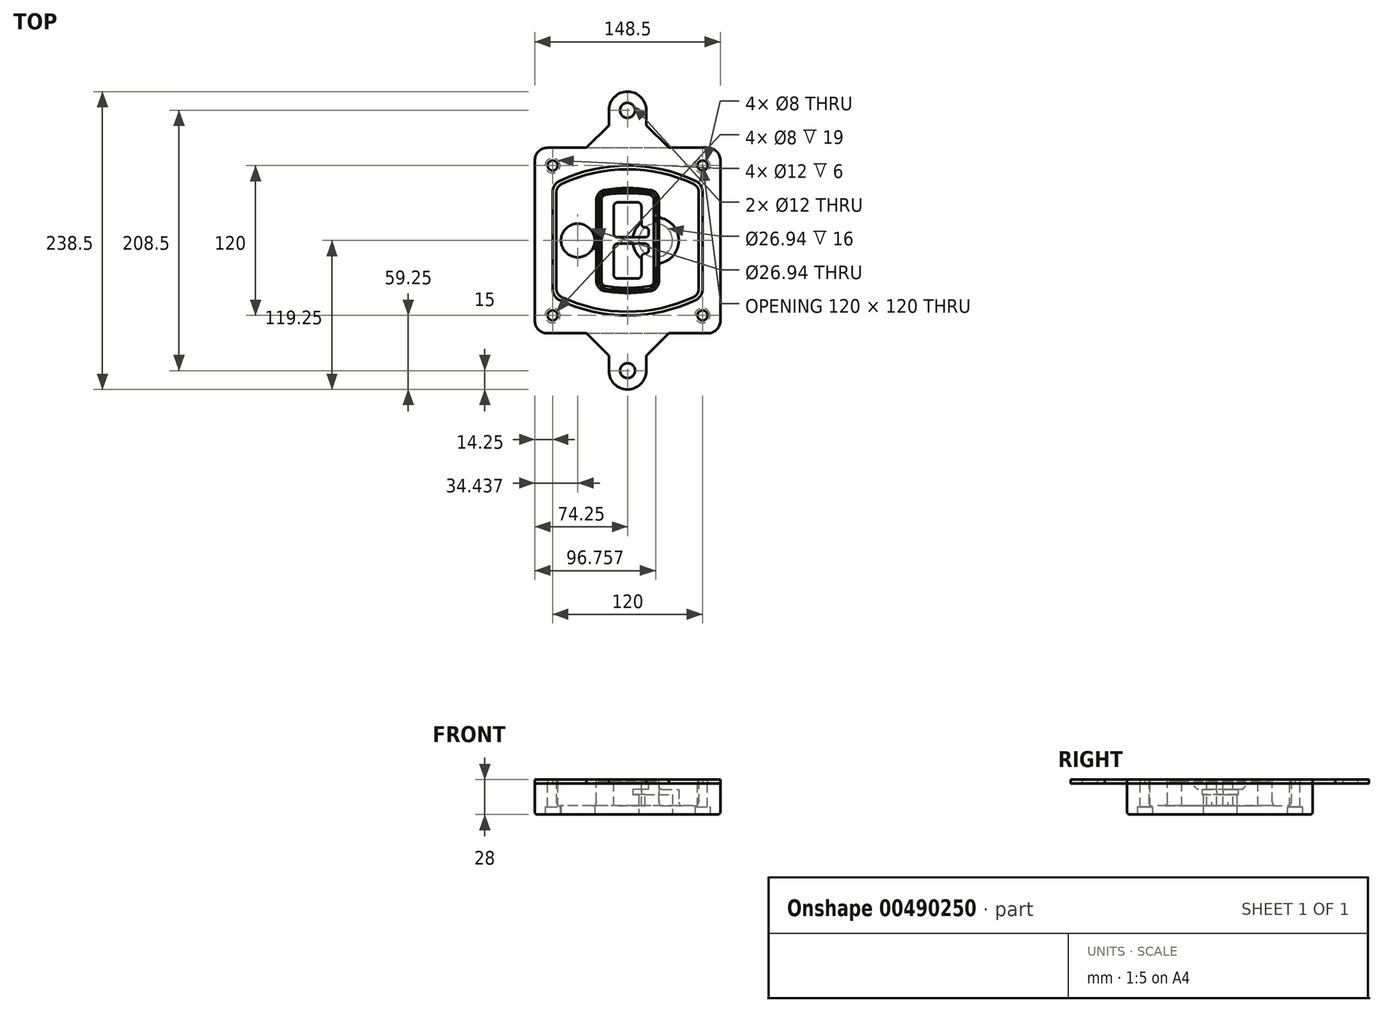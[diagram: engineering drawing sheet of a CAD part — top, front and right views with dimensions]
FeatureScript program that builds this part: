
annotation { "Feature Type Name" : "Feature", "Feature Type Description" : "" }
export const myFeature = defineFeature(function(context is Context, id is Id, definition is map)
    precondition{}
    {
        {
            var Q0;
            Q0=qCreatedBy(makeId("Top.planeOp"),FACE);
            var sketch = newSketch(context, id + "F0", { "sketchPlane" : qUnion([Q0])});
            skPoint(sketch, "E0.rect.middle", {"position": v(0, 0) * mm});
            skLineSegment(sketch, "E1.bottom", {"start": v(-64.25, -74.25) * mm, "end": v(64.25, -74.25) * mm});
            skLineSegment(sketch, "E1.top", {"start": v(-64.25, 74.25) * mm, "end": v(64.25, 74.25) * mm});
            skLineSegment(sketch, "E1.left", {"start": v(-74.25, -64.25) * mm, "end": v(-74.25, 64.25) * mm});
            skLineSegment(sketch, "E1.right", {"start": v(74.25, -64.25) * mm, "end": v(74.25, 64.25) * mm});
            skLineSegment(sketch, "E2", {"start": v(-74.25, 74.25) * mm, "end": v(74.25, -74.25) * mm, "construction": true});
            skLineSegment(sketch, "E3", {"start": v(74.25, 74.25) * mm, "end": v(-74.25, -74.25) * mm, "construction": true});
            skCircle(sketch, "E4", {"center": v(-60, 60) * mm, "radius": 4 * mm});
            skCircle(sketch, "E5", {"center": v(60, 60) * mm, "radius": 4 * mm});
            skCircle(sketch, "E6", {"center": v(60, -60) * mm, "radius": 4 * mm});
            skCircle(sketch, "E7", {"center": v(-60, -60) * mm, "radius": 4 * mm});
            skLineSegment(sketch, "E8", {"start": v(-60, 60) * mm, "end": v(60, 60) * mm, "construction": true});
            skLineSegment(sketch, "E9", {"start": v(60, 60) * mm, "end": v(60, -60) * mm, "construction": true});
            skLineSegment(sketch, "E10", {"start": v(60, -60) * mm, "end": v(-60, -60) * mm, "construction": true});
            skLineSegment(sketch, "E11", {"start": v(-60, -60) * mm, "end": v(-60, 60) * mm, "construction": true});
            skLineSegment(sketch, "E12", {"start": v(-60, 38.83) * mm, "end": v(-60, -38.83) * mm});
            skLineSegment(sketch, "E13", {"start": v(60, 38.83) * mm, "end": v(60, -38.83) * mm});
            skArc(sketch, "E14", {"start": v(54.26, 47.88) * mm, "mid": v(0, 60) * mm, "end": v(-54.26, 47.88) * mm});
            skArc(sketch, "E15", {"start": v(-54.26, -47.88) * mm, "mid": v(0, -60) * mm, "end": v(54.26, -47.88) * mm});
            skLineSegment(sketch, "E16", {"start": v(-60, 0) * mm, "end": v(60, 0) * mm, "construction": true});
            skPoint(sketch, "E17.visualSharp", {"position": v(-60, -45) * mm});
            skArc(sketch, "E17.filletArc", {"start": v(-60, -38.83) * mm, "mid": v(-58.44, -44.2) * mm, "end": v(-54.26, -47.88) * mm});
            skPoint(sketch, "E18.visualSharp", {"position": v(-60, 45) * mm});
            skArc(sketch, "E18.filletArc", {"start": v(-54.26, 47.88) * mm, "mid": v(-58.44, 44.2) * mm, "end": v(-60, 38.83) * mm});
            skPoint(sketch, "E19.visualSharp", {"position": v(60, 45) * mm});
            skArc(sketch, "E19.filletArc", {"start": v(60, 38.83) * mm, "mid": v(58.44, 44.2) * mm, "end": v(54.26, 47.88) * mm});
            skPoint(sketch, "E20.visualSharp", {"position": v(60, -45) * mm});
            skArc(sketch, "E20.filletArc", {"start": v(54.26, -47.88) * mm, "mid": v(58.44, -44.2) * mm, "end": v(60, -38.83) * mm});
            skPoint(sketch, "E21.visualSharp", {"position": v(-74.25, 74.25) * mm});
            skArc(sketch, "E21.filletArc", {"start": v(-64.25, 74.25) * mm, "mid": v(-71.32, 71.32) * mm, "end": v(-74.25, 64.25) * mm});
            skPoint(sketch, "E22.visualSharp", {"position": v(74.25, 74.25) * mm});
            skArc(sketch, "E22.filletArc", {"start": v(74.25, 64.25) * mm, "mid": v(71.32, 71.32) * mm, "end": v(64.25, 74.25) * mm});
            skPoint(sketch, "E23.visualSharp", {"position": v(74.25, -74.25) * mm});
            skArc(sketch, "E23.filletArc", {"start": v(64.25, -74.25) * mm, "mid": v(71.32, -71.32) * mm, "end": v(74.25, -64.25) * mm});
            skPoint(sketch, "E24.visualSharp", {"position": v(-74.25, -74.25) * mm});
            skArc(sketch, "E24.filletArc", {"start": v(-74.25, -64.25) * mm, "mid": v(-71.32, -71.32) * mm, "end": v(-64.25, -74.25) * mm});
            skArc(sketch, "E25.0", {"start": v(57, 38.83) * mm, "mid": v(55.9, 42.58) * mm, "end": v(52.98, 45.17) * mm});
            skLineSegment(sketch, "E25.1", {"start": v(57, 38.83) * mm, "end": v(57, -38.83) * mm});
            skArc(sketch, "E25.2", {"start": v(52.98, -45.17) * mm, "mid": v(55.9, -42.58) * mm, "end": v(57, -38.83) * mm});
            skArc(sketch, "E25.3", {"start": v(-52.98, -45.17) * mm, "mid": v(0, -57) * mm, "end": v(52.98, -45.17) * mm});
            skArc(sketch, "E25.4", {"start": v(-57, -38.83) * mm, "mid": v(-55.9, -42.58) * mm, "end": v(-52.98, -45.17) * mm});
            skArc(sketch, "E25.5", {"start": v(52.98, 45.17) * mm, "mid": v(0, 57) * mm, "end": v(-52.98, 45.17) * mm});
            skLineSegment(sketch, "E25.6", {"start": v(-57, 38.83) * mm, "end": v(-57, -38.83) * mm});
            skArc(sketch, "E25.7", {"start": v(-52.98, 45.17) * mm, "mid": v(-55.9, 42.58) * mm, "end": v(-57, 38.83) * mm});
            skArc(sketch, "E26.0", {"start": v(-55.96, 51.5) * mm, "mid": v(-61.82, 46.33) * mm, "end": v(-64, 38.83) * mm});
            skArc(sketch, "E26.1", {"start": v(55.96, 51.5) * mm, "mid": v(0, 64) * mm, "end": v(-55.96, 51.5) * mm});
            skArc(sketch, "E26.2", {"start": v(64, 38.83) * mm, "mid": v(61.82, 46.33) * mm, "end": v(55.96, 51.5) * mm});
            skLineSegment(sketch, "E26.3", {"start": v(64, 38.83) * mm, "end": v(64, -38.83) * mm});
            skArc(sketch, "E26.4", {"start": v(55.96, -51.5) * mm, "mid": v(61.82, -46.33) * mm, "end": v(64, -38.83) * mm});
            skLineSegment(sketch, "E26.5", {"start": v(-64, 38.83) * mm, "end": v(-64, -38.83) * mm});
            skArc(sketch, "E26.6", {"start": v(-55.96, -51.5) * mm, "mid": v(0, -64) * mm, "end": v(55.96, -51.5) * mm});
            skArc(sketch, "E26.7", {"start": v(-64, -38.83) * mm, "mid": v(-61.82, -46.33) * mm, "end": v(-55.96, -51.5) * mm});
            skSolve(sketch);
        }
        {
            var Q0;
            Q0=makeQuery(id+"F0.imprint","IMPRINT",FACE,{"disambiguationData":[TD([[makeQuery(id+"F0.imprint","IMPRINT",EDGE,{"derivedFrom":sQuery(id+"F0.wireOp",EDGE,"E1.bottom")}),1.0]])]});
            var Q1;
            Q1=makeQuery(id+"F0.imprint","IMPRINT",FACE,{"disambiguationData":[TD([[makeQuery(id+"F0.imprint","IMPRINT",EDGE,{"derivedFrom":sQuery(id+"F0.wireOp",EDGE,"E12")}),1.0]])]});
            var Q2;
            Q2=makeQuery(id+"F0.imprint","IMPRINT",FACE,{"disambiguationData":[TD([[makeQuery(id+"F0.imprint","IMPRINT",EDGE,{"derivedFrom":sQuery(id+"F0.wireOp",EDGE,"E25.0")}),1.0]])]});
            var Q3;
            Q3=makeQuery(id+"F0.imprint","IMPRINT",FACE,{"disambiguationData":[TD([[makeQuery(id+"F0.imprint","IMPRINT",EDGE,{"derivedFrom":sQuery(id+"F0.wireOp",EDGE,"E12")}),-1.0]])]});
            extrude(context, id + "F1", {"entities" : qUnion([Q0, Q1, Q2, Q3]), "oppositeDirection" : true, "depth" : 25 * mm});
        }
        {
            var Q0;
            Q0=makeQuery(id+"F0.imprint","IMPRINT",FACE,{"disambiguationData":[TD([[makeQuery(id+"F0.imprint","IMPRINT",EDGE,{"derivedFrom":sQuery(id+"F0.wireOp",EDGE,"E12")}),1.0]])]});
            extrude(context, id + "F2", {"entities" : qUnion([Q0]), "operationType" : NewBodyOperationType.ADD, "depth" : 3 * mm});
        }
        {
            var Q0;
            Q0=makeQuery(id+"F0.imprint","IMPRINT",FACE,{"disambiguationData":[TD([[makeQuery(id+"F0.imprint","IMPRINT",EDGE,{"derivedFrom":sQuery(id+"F0.wireOp",EDGE,"E25.0")}),1.0]])]});
            extrude(context, id + "F3", {"entities" : qUnion([Q0]), "operationType" : NewBodyOperationType.REMOVE, "oppositeDirection" : true, "depth" : 18 * mm});
        }
        {
            var Q0;
            Q0=makeQuery(id+"F2.opExtrude","CAP_FACE",FACE,{"disambiguationData":[OSD([sQuery(id+"F0.wireOp",EDGE,"E12"),sQuery(id+"F0.wireOp",EDGE,"E13"),sQuery(id+"F0.wireOp",EDGE,"E14"),sQuery(id+"F0.wireOp",EDGE,"E15"),sQuery(id+"F0.wireOp",EDGE,"E17.filletArc"),sQuery(id+"F0.wireOp",EDGE,"E18.filletArc"),sQuery(id+"F0.wireOp",EDGE,"E19.filletArc"),sQuery(id+"F0.wireOp",EDGE,"E20.filletArc"),sQuery(id+"F0.wireOp",EDGE,"E25.0"),sQuery(id+"F0.wireOp",EDGE,"E25.1"),sQuery(id+"F0.wireOp",EDGE,"E25.2"),sQuery(id+"F0.wireOp",EDGE,"E25.3"),sQuery(id+"F0.wireOp",EDGE,"E25.4"),sQuery(id+"F0.wireOp",EDGE,"E25.5"),sQuery(id+"F0.wireOp",EDGE,"E25.6"),sQuery(id+"F0.wireOp",EDGE,"E25.7")])],"isStart":false});
            var sketch = newSketch(context, id + "F4", { "sketchPlane" : qUnion([Q0])});
            skArc(sketch, "E27.0", {"start": v(-18.34, -40.45) * mm, "mid": v(0, -42) * mm, "end": v(18.34, -40.45) * mm});
            skArc(sketch, "E28.0", {"start": v(18.34, 40.45) * mm, "mid": v(0, 42) * mm, "end": v(-18.34, 40.45) * mm});
            skLineSegment(sketch, "E29", {"start": v(-25, 32.57) * mm, "end": v(-25, -32.57) * mm});
            skLineSegment(sketch, "E30", {"start": v(25, 32.57) * mm, "end": v(25, -32.57) * mm});
            skLineSegment(sketch, "E31", {"start": v(-25, 39.1) * mm, "end": v(25, 39.1) * mm, "construction": true});
            skLineSegment(sketch, "E32", {"start": v(-25, -39.1) * mm, "end": v(25, -39.1) * mm, "construction": true});
            skPoint(sketch, "E33.visualSharp", {"position": v(-25, 39.1) * mm});
            skArc(sketch, "E33.filletArc", {"start": v(-18.34, 40.45) * mm, "mid": v(-23.11, 37.73) * mm, "end": v(-25, 32.57) * mm});
            skPoint(sketch, "E34.visualSharp", {"position": v(25, 39.1) * mm});
            skArc(sketch, "E34.filletArc", {"start": v(25, 32.57) * mm, "mid": v(23.11, 37.73) * mm, "end": v(18.34, 40.45) * mm});
            skPoint(sketch, "E35.visualSharp", {"position": v(25, -39.1) * mm});
            skArc(sketch, "E35.filletArc", {"start": v(18.34, -40.45) * mm, "mid": v(23.11, -37.73) * mm, "end": v(25, -32.57) * mm});
            skPoint(sketch, "E36.visualSharp", {"position": v(-25, -39.1) * mm});
            skArc(sketch, "E36.filletArc", {"start": v(-25, -32.57) * mm, "mid": v(-23.11, -37.73) * mm, "end": v(-18.34, -40.45) * mm});
            skArc(sketch, "E37.0", {"start": v(52.98, 45.17) * mm, "mid": v(0, 57) * mm, "end": v(-52.98, 45.17) * mm});
            skArc(sketch, "E37.1", {"start": v(-52.98, 45.17) * mm, "mid": v(-55.9, 42.58) * mm, "end": v(-57, 38.83) * mm});
            skLineSegment(sketch, "E37.2", {"start": v(-57, 38.83) * mm, "end": v(-57, -38.83) * mm});
            skArc(sketch, "E37.3", {"start": v(-57, -38.83) * mm, "mid": v(-55.9, -42.58) * mm, "end": v(-52.98, -45.17) * mm});
            skArc(sketch, "E37.4", {"start": v(-52.98, -45.17) * mm, "mid": v(0, -57) * mm, "end": v(52.98, -45.17) * mm});
            skArc(sketch, "E37.5", {"start": v(52.98, -45.17) * mm, "mid": v(55.9, -42.58) * mm, "end": v(57, -38.83) * mm});
            skLineSegment(sketch, "E37.6", {"start": v(57, 38.83) * mm, "end": v(57, -38.83) * mm});
            skArc(sketch, "E37.7", {"start": v(57, 38.83) * mm, "mid": v(55.9, 42.58) * mm, "end": v(52.98, 45.17) * mm});
            skLineSegment(sketch, "E38.0", {"start": v(23, 32.57) * mm, "end": v(23, -32.57) * mm});
            skArc(sketch, "E38.1", {"start": v(18, -38.48) * mm, "mid": v(21.58, -36.44) * mm, "end": v(23, -32.57) * mm});
            skArc(sketch, "E38.2", {"start": v(-18, -38.48) * mm, "mid": v(0, -40) * mm, "end": v(18, -38.48) * mm});
            skArc(sketch, "E38.3", {"start": v(-23, -32.57) * mm, "mid": v(-21.58, -36.44) * mm, "end": v(-18, -38.48) * mm});
            skLineSegment(sketch, "E38.4", {"start": v(-23, 32.57) * mm, "end": v(-23, -32.57) * mm});
            skArc(sketch, "E38.5", {"start": v(23, 32.57) * mm, "mid": v(21.58, 36.44) * mm, "end": v(18, 38.48) * mm});
            skArc(sketch, "E38.6", {"start": v(-18, 38.48) * mm, "mid": v(-21.58, 36.44) * mm, "end": v(-23, 32.57) * mm});
            skArc(sketch, "E38.7", {"start": v(18, 38.48) * mm, "mid": v(0, 40) * mm, "end": v(-18, 38.48) * mm});
            skArc(sketch, "E39.0", {"start": v(21, 32.57) * mm, "mid": v(20.06, 35.15) * mm, "end": v(17.67, 36.5) * mm});
            skLineSegment(sketch, "E39.1", {"start": v(21, 32.57) * mm, "end": v(21, -32.57) * mm});
            skArc(sketch, "E39.2", {"start": v(17.67, -36.5) * mm, "mid": v(20.06, -35.15) * mm, "end": v(21, -32.57) * mm});
            skArc(sketch, "E39.3", {"start": v(-17.67, -36.5) * mm, "mid": v(0, -38) * mm, "end": v(17.67, -36.5) * mm});
            skArc(sketch, "E39.4", {"start": v(-21, -32.57) * mm, "mid": v(-20.06, -35.15) * mm, "end": v(-17.67, -36.5) * mm});
            skArc(sketch, "E39.5", {"start": v(17.67, 36.5) * mm, "mid": v(0, 38) * mm, "end": v(-17.67, 36.5) * mm});
            skLineSegment(sketch, "E39.6", {"start": v(-21, 32.57) * mm, "end": v(-21, -32.57) * mm});
            skArc(sketch, "E39.7", {"start": v(-17.67, 36.5) * mm, "mid": v(-20.06, 35.15) * mm, "end": v(-21, 32.57) * mm});
            skLineSegment(sketch, "E40", {"start": v(-25, 0) * mm, "end": v(25, 0) * mm, "construction": true});
            skLineSegment(sketch, "E41", {"start": v(-11, 5.5) * mm, "end": v(-11, 27.5) * mm});
            skLineSegment(sketch, "E42", {"start": v(-8, 30.5) * mm, "end": v(8, 30.5) * mm});
            skLineSegment(sketch, "E43", {"start": v(11, 27.5) * mm, "end": v(11, 13.5) * mm});
            skLineSegment(sketch, "E44", {"start": v(14, 10.5) * mm, "end": v(14, 10.5) * mm});
            skLineSegment(sketch, "E45", {"start": v(17, 7.5) * mm, "end": v(17, 5.5) * mm});
            skLineSegment(sketch, "E46", {"start": v(14, 2.5) * mm, "end": v(-8, 2.5) * mm});
            skPoint(sketch, "E47.visualSharp", {"position": v(-11, 30.5) * mm});
            skArc(sketch, "E47.filletArc", {"start": v(-8, 30.5) * mm, "mid": v(-10.12, 29.62) * mm, "end": v(-11, 27.5) * mm});
            skPoint(sketch, "E48.visualSharp", {"position": v(11, 30.5) * mm});
            skArc(sketch, "E48.filletArc", {"start": v(11, 27.5) * mm, "mid": v(10.12, 29.62) * mm, "end": v(8, 30.5) * mm});
            skPoint(sketch, "E49.visualSharp", {"position": v(11, 10.5) * mm});
            skArc(sketch, "E49.filletArc", {"start": v(11, 13.5) * mm, "mid": v(11.88, 11.38) * mm, "end": v(14, 10.5) * mm});
            skPoint(sketch, "E50.visualSharp", {"position": v(17, 10.5) * mm});
            skArc(sketch, "E50.filletArc", {"start": v(17, 7.5) * mm, "mid": v(16.12, 9.62) * mm, "end": v(14, 10.5) * mm});
            skPoint(sketch, "E51.visualSharp", {"position": v(17, 2.5) * mm});
            skArc(sketch, "E51.filletArc", {"start": v(14, 2.5) * mm, "mid": v(16.12, 3.38) * mm, "end": v(17, 5.5) * mm});
            skPoint(sketch, "E52.visualSharp", {"position": v(-11, 2.5) * mm});
            skArc(sketch, "E52.filletArc", {"start": v(-11, 5.5) * mm, "mid": v(-10.12, 3.38) * mm, "end": v(-8, 2.5) * mm});
            skLineSegment(sketch, "E53.0.MirrorCS", {"start": v(14, -2.5) * mm, "end": v(-8, -2.5) * mm});
            skArc(sketch, "E54.0.MirrorCS", {"start": v(-11, -5.5) * mm, "mid": v(-10.12, -3.38) * mm, "end": v(-8, -2.5) * mm});
            skLineSegment(sketch, "E55.0.MirrorCS", {"start": v(-11, -5.5) * mm, "end": v(-11, -27.5) * mm});
            skArc(sketch, "E56.0.MirrorCS", {"start": v(-8, -30.5) * mm, "mid": v(-10.12, -29.62) * mm, "end": v(-11, -27.5) * mm});
            skLineSegment(sketch, "E57.0.MirrorCS", {"start": v(-8, -30.5) * mm, "end": v(8, -30.5) * mm});
            skArc(sketch, "E58.0.MirrorCS", {"start": v(11, -27.5) * mm, "mid": v(10.12, -29.62) * mm, "end": v(8, -30.5) * mm});
            skLineSegment(sketch, "E59.0.MirrorCS", {"start": v(11, -27.5) * mm, "end": v(11, -13.5) * mm});
            skArc(sketch, "E60.0.MirrorCS", {"start": v(11, -13.5) * mm, "mid": v(11.88, -11.38) * mm, "end": v(14, -10.5) * mm});
            skArc(sketch, "E61.0.MirrorCS", {"start": v(17, -7.5) * mm, "mid": v(16.12, -9.62) * mm, "end": v(14, -10.5) * mm});
            skLineSegment(sketch, "E62.0.MirrorCS", {"start": v(17, -7.5) * mm, "end": v(17, -5.5) * mm});
            skArc(sketch, "E63.0.MirrorCS", {"start": v(14, -2.5) * mm, "mid": v(16.12, -3.38) * mm, "end": v(17, -5.5) * mm});
            skSolve(sketch);
        }
        {
            var Q0;
            Q0=makeQuery(id+"F4.imprint","IMPRINT",FACE,{"disambiguationData":[TD([[makeQuery(id+"F4.imprint","IMPRINT",EDGE,{"derivedFrom":sQuery(id+"F4.wireOp",EDGE,"E27.0")}),1.0]])]});
            var Q1;
            Q1=makeQuery(id+"F4.imprint","IMPRINT",FACE,{"disambiguationData":[TD([[makeQuery(id+"F4.imprint","IMPRINT",EDGE,{"derivedFrom":sQuery(id+"F4.wireOp",EDGE,"E38.0")}),-1.0]])]});
            var Q2;
            Q2=makeQuery(id+"F4.imprint","IMPRINT",FACE,{"disambiguationData":[TD([[makeQuery(id+"F4.imprint","IMPRINT",EDGE,{"derivedFrom":sQuery(id+"F4.wireOp",EDGE,"E39.0")}),1.0]])]});
            extrude(context, id + "F5", {"entities" : qUnion([Q0, Q1, Q2]), "operationType" : NewBodyOperationType.ADD, "endBound" : BoundingType.UP_TO_NEXT, "oppositeDirection" : true, "depth" : 25 * mm});
        }
        {
            var Q0;
            Q0=makeQuery(id+"F4.imprint","IMPRINT",FACE,{"disambiguationData":[TD([[makeQuery(id+"F4.imprint","IMPRINT",EDGE,{"derivedFrom":sQuery(id+"F4.wireOp",EDGE,"E38.0")}),-1.0]])]});
            extrude(context, id + "F6", {"entities" : qUnion([Q0]), "operationType" : NewBodyOperationType.REMOVE, "oppositeDirection" : true, "depth" : 2 * mm});
        }
        {
            var Q0;
            Q0=makeQuery(id+"F1.opExtrude","CAP_FACE",FACE,{"disambiguationData":[OSD([sQuery(id+"F0.wireOp",EDGE,"E1.bottom"),sQuery(id+"F0.wireOp",EDGE,"E1.top"),sQuery(id+"F0.wireOp",EDGE,"E1.left"),sQuery(id+"F0.wireOp",EDGE,"E1.right"),sQuery(id+"F0.wireOp",EDGE,"E4"),sQuery(id+"F0.wireOp",EDGE,"E5"),sQuery(id+"F0.wireOp",EDGE,"E6"),sQuery(id+"F0.wireOp",EDGE,"E7"),sQuery(id+"F0.wireOp",EDGE,"E21.filletArc"),sQuery(id+"F0.wireOp",EDGE,"E22.filletArc"),sQuery(id+"F0.wireOp",EDGE,"E23.filletArc"),sQuery(id+"F0.wireOp",EDGE,"E24.filletArc")])],"isStart":false});
            var sketch = newSketch(context, id + "F7", { "sketchPlane" : qUnion([Q0])});
            skCircle(sketch, "E64", {"center": v(22.5, 0) * mm, "radius": 13.47 * mm});
            skCircle(sketch, "E65", {"center": v(-39.81, 0) * mm, "radius": 13.47 * mm});
            skLineSegment(sketch, "E66", {"start": v(74.25, 0) * mm, "end": v(-74.25, 0) * mm});
            skCircle(sketch, "E67", {"center": v(22.5, 0) * mm, "radius": 18.47 * mm});
            skCircle(sketch, "E68", {"center": v(60, -60) * mm, "radius": 6 * mm});
            skCircle(sketch, "E69", {"center": v(-60, -60) * mm, "radius": 6 * mm});
            skCircle(sketch, "E70", {"center": v(-60, 60) * mm, "radius": 6 * mm});
            skCircle(sketch, "E71", {"center": v(60, 60) * mm, "radius": 6 * mm});
            skSolve(sketch);
        }
        {
            var Q0;
            {var subQ1=sQuery(id+"F7.wireOp",EDGE,"E66");var subQ4=sQuery(id+"F7.wireOp",EDGE,"E64");var subQ6=makeQuery(id+"F7.imprint","INTERSECT",VERTEX,{"disambiguationData":[OD(0.0)],"derivedFrom":[subQ4,subQ1]});Q0=makeQuery(id+"F7.imprint","IMPRINT",FACE,{"disambiguationData":[TD([[makeQuery(id+"F7.imprint","IMPRINT",EDGE,{"disambiguationData":[TD([[subQ6,-1.0]])],"derivedFrom":subQ4}),-1.0]])]});}
            var Q1;
            {var subQ0=sQuery(id+"F7.wireOp",EDGE,"E66");var subQ1=sQuery(id+"F7.wireOp",EDGE,"E64");var subQ3=makeQuery(id+"F7.imprint","INTERSECT",VERTEX,{"disambiguationData":[OD(0.0)],"derivedFrom":[subQ1,subQ0]});Q1=makeQuery(id+"F7.imprint","IMPRINT",FACE,{"disambiguationData":[TD([[makeQuery(id+"F7.imprint","IMPRINT",EDGE,{"disambiguationData":[TD([[subQ3,-1.0]])],"derivedFrom":subQ1}),1.0]])]});}
            var Q2;
            {var subQ0=sQuery(id+"F7.wireOp",EDGE,"E66");var subQ1=sQuery(id+"F7.wireOp",EDGE,"E64");var subQ3=makeQuery(id+"F7.imprint","INTERSECT",VERTEX,{"disambiguationData":[OD(0.0)],"derivedFrom":[subQ1,subQ0]});Q2=makeQuery(id+"F7.imprint","IMPRINT",FACE,{"disambiguationData":[TD([[makeQuery(id+"F7.imprint","IMPRINT",EDGE,{"disambiguationData":[TD([[subQ3,1.0]])],"derivedFrom":subQ1}),1.0]])]});}
            var Q3;
            {var subQ1=sQuery(id+"F7.wireOp",EDGE,"E66");var subQ4=sQuery(id+"F7.wireOp",EDGE,"E64");var subQ6=makeQuery(id+"F7.imprint","INTERSECT",VERTEX,{"disambiguationData":[OD(0.0)],"derivedFrom":[subQ4,subQ1]});Q3=makeQuery(id+"F7.imprint","IMPRINT",FACE,{"disambiguationData":[TD([[makeQuery(id+"F7.imprint","IMPRINT",EDGE,{"disambiguationData":[TD([[subQ6,1.0]])],"derivedFrom":subQ4}),-1.0]])]});}
            extrude(context, id + "F8", {"entities" : qUnion([Q0, Q1, Q2, Q3]), "operationType" : NewBodyOperationType.ADD, "oppositeDirection" : true, "depth" : 20 * mm});
        }
        {
            var Q0;
            {var subQ0=sQuery(id+"F7.wireOp",EDGE,"E66");var subQ1=sQuery(id+"F7.wireOp",EDGE,"E64");var subQ3=makeQuery(id+"F7.imprint","INTERSECT",VERTEX,{"disambiguationData":[OD(0.0)],"derivedFrom":[subQ1,subQ0]});Q0=makeQuery(id+"F7.imprint","IMPRINT",FACE,{"disambiguationData":[TD([[makeQuery(id+"F7.imprint","IMPRINT",EDGE,{"disambiguationData":[TD([[subQ3,-1.0]])],"derivedFrom":subQ1}),1.0]])]});}
            var Q1;
            {var subQ0=sQuery(id+"F7.wireOp",EDGE,"E66");var subQ1=sQuery(id+"F7.wireOp",EDGE,"E64");var subQ3=makeQuery(id+"F7.imprint","INTERSECT",VERTEX,{"disambiguationData":[OD(0.0)],"derivedFrom":[subQ1,subQ0]});Q1=makeQuery(id+"F7.imprint","IMPRINT",FACE,{"disambiguationData":[TD([[makeQuery(id+"F7.imprint","IMPRINT",EDGE,{"disambiguationData":[TD([[subQ3,1.0]])],"derivedFrom":subQ1}),1.0]])]});}
            extrude(context, id + "F9", {"entities" : qUnion([Q0, Q1]), "operationType" : NewBodyOperationType.REMOVE, "oppositeDirection" : true, "depth" : 16 * mm});
        }
        {
            var Q0;
            {var subQ0=sQuery(id+"F7.wireOp",EDGE,"E66");var subQ1=sQuery(id+"F7.wireOp",EDGE,"E65");var subQ3=makeQuery(id+"F7.imprint","INTERSECT",VERTEX,{"disambiguationData":[OD(0.0)],"derivedFrom":[subQ1,subQ0]});Q0=makeQuery(id+"F7.imprint","IMPRINT",FACE,{"disambiguationData":[TD([[makeQuery(id+"F7.imprint","IMPRINT",EDGE,{"disambiguationData":[TD([[subQ3,-1.0]])],"derivedFrom":subQ1}),1.0]])]});}
            var Q1;
            {var subQ0=sQuery(id+"F7.wireOp",EDGE,"E66");var subQ1=sQuery(id+"F7.wireOp",EDGE,"E65");var subQ3=makeQuery(id+"F7.imprint","INTERSECT",VERTEX,{"disambiguationData":[OD(0.0)],"derivedFrom":[subQ1,subQ0]});Q1=makeQuery(id+"F7.imprint","IMPRINT",FACE,{"disambiguationData":[TD([[makeQuery(id+"F7.imprint","IMPRINT",EDGE,{"disambiguationData":[TD([[subQ3,1.0]])],"derivedFrom":subQ1}),1.0]])]});}
            extrude(context, id + "F10", {"entities" : qUnion([Q0, Q1]), "operationType" : NewBodyOperationType.REMOVE, "oppositeDirection" : true, "depth" : 25 * mm});
        }
        {
            var Q0;
            Q0=makeQuery(id+"F7.imprint","IMPRINT",FACE,{"disambiguationData":[TD([[makeQuery(id+"F7.imprint","IMPRINT",EDGE,{"derivedFrom":sQuery(id+"F7.wireOp",EDGE,"E68")}),1.0]])]});
            var Q1;
            Q1=makeQuery(id+"F7.imprint","IMPRINT",FACE,{"disambiguationData":[TD([[makeQuery(id+"F7.imprint","IMPRINT",EDGE,{"derivedFrom":makeQuery(id+"F1.opExtrude","CAP_EDGE",EDGE,{"disambiguationData":[OSD([sQuery(id+"F0.wireOp",EDGE,"E5")])],"isStart":false})}),-1.0]])]});
            var Q2;
            Q2=makeQuery(id+"F7.imprint","IMPRINT",FACE,{"disambiguationData":[TD([[makeQuery(id+"F7.imprint","IMPRINT",EDGE,{"derivedFrom":sQuery(id+"F7.wireOp",EDGE,"E69")}),1.0]])]});
            var Q3;
            Q3=makeQuery(id+"F7.imprint","IMPRINT",FACE,{"disambiguationData":[TD([[makeQuery(id+"F7.imprint","IMPRINT",EDGE,{"derivedFrom":makeQuery(id+"F1.opExtrude","CAP_EDGE",EDGE,{"disambiguationData":[OSD([sQuery(id+"F0.wireOp",EDGE,"E4")])],"isStart":false})}),-1.0]])]});
            var Q4;
            Q4=makeQuery(id+"F7.imprint","IMPRINT",FACE,{"disambiguationData":[TD([[makeQuery(id+"F7.imprint","IMPRINT",EDGE,{"derivedFrom":sQuery(id+"F7.wireOp",EDGE,"E70")}),1.0]])]});
            var Q5;
            Q5=makeQuery(id+"F7.imprint","IMPRINT",FACE,{"disambiguationData":[TD([[makeQuery(id+"F7.imprint","IMPRINT",EDGE,{"derivedFrom":makeQuery(id+"F1.opExtrude","CAP_EDGE",EDGE,{"disambiguationData":[OSD([sQuery(id+"F0.wireOp",EDGE,"E7")])],"isStart":false})}),-1.0]])]});
            var Q6;
            Q6=makeQuery(id+"F7.imprint","IMPRINT",FACE,{"disambiguationData":[TD([[makeQuery(id+"F7.imprint","IMPRINT",EDGE,{"derivedFrom":sQuery(id+"F7.wireOp",EDGE,"E71")}),1.0]])]});
            var Q7;
            Q7=makeQuery(id+"F7.imprint","IMPRINT",FACE,{"disambiguationData":[TD([[makeQuery(id+"F7.imprint","IMPRINT",EDGE,{"derivedFrom":makeQuery(id+"F1.opExtrude","CAP_EDGE",EDGE,{"disambiguationData":[OSD([sQuery(id+"F0.wireOp",EDGE,"E6")])],"isStart":false})}),-1.0]])]});
            extrude(context, id + "F11", {"entities" : qUnion([Q0, Q1, Q2, Q3, Q4, Q5, Q6, Q7]), "operationType" : NewBodyOperationType.REMOVE, "oppositeDirection" : true, "depth" : 6 * mm});
        }
        {
            var Q0;
            Q0=makeQuery(id+"F9.boolean.opBoolean","COPY",FACE,{"derivedFrom":makeQuery(id+"F9.opExtrude","CAP_FACE",FACE,{"disambiguationData":[OSD([sQuery(id+"F7.wireOp",EDGE,"E64")])],"isStart":false})});
            var sketch = newSketch(context, id + "F12", { "sketchPlane" : qUnion([Q0])});
            skArc(sketch, "E72.0", {"start": v(11, 14.45) * mm, "mid": v(6.45, 9.13) * mm, "end": v(4.2, 2.5) * mm});
            skArc(sketch, "E72.1", {"start": v(4.2, -2.5) * mm, "mid": v(6.45, -9.13) * mm, "end": v(11, -14.45) * mm});
            skLineSegment(sketch, "E73", {"start": v(4.2, -2.5) * mm, "end": v(14, -2.5) * mm});
            skLineSegment(sketch, "E74.0", {"start": v(14, 2.5) * mm, "end": v(4.2, 2.5) * mm});
            skArc(sketch, "E74.1", {"start": v(14, 2.5) * mm, "mid": v(16.12, 3.38) * mm, "end": v(17, 5.5) * mm});
            skLineSegment(sketch, "E74.2", {"start": v(17, 7.5) * mm, "end": v(17, 5.5) * mm});
            skArc(sketch, "E74.3", {"start": v(17, 7.5) * mm, "mid": v(16.12, 9.62) * mm, "end": v(14, 10.5) * mm});
            skArc(sketch, "E74.4", {"start": v(11, 13.5) * mm, "mid": v(11.88, 11.38) * mm, "end": v(14, 10.5) * mm});
            skLineSegment(sketch, "E74.5", {"start": v(11, 14.45) * mm, "end": v(11, 13.5) * mm});
            skLineSegment(sketch, "E74.7", {"start": v(14, -2.5) * mm, "end": v(4.2, -2.5) * mm});
            skArc(sketch, "E74.8", {"start": v(14, -2.5) * mm, "mid": v(16.12, -3.38) * mm, "end": v(17, -5.5) * mm});
            skLineSegment(sketch, "E74.9", {"start": v(17, -7.5) * mm, "end": v(17, -5.5) * mm});
            skArc(sketch, "E74.10", {"start": v(17, -7.5) * mm, "mid": v(16.12, -9.62) * mm, "end": v(14, -10.5) * mm});
            skArc(sketch, "E74.11", {"start": v(11, -13.5) * mm, "mid": v(11.88, -11.38) * mm, "end": v(14, -10.5) * mm});
            skLineSegment(sketch, "E74.12", {"start": v(11, -14.45) * mm, "end": v(11, -13.5) * mm});
            skPoint(sketch, "E75.orphan", {"position": v(11, -27.5) * mm});
            skPoint(sketch, "E76.orphan", {"position": v(-8, -2.5) * mm});
            skPoint(sketch, "E77.orphan", {"position": v(-8, 2.5) * mm});
            skPoint(sketch, "E78.orphan", {"position": v(11, 27.5) * mm});
            skSolve(sketch);
        }
        {
            var Q0;
            {var subQ7=sQuery(id+"F12.wireOp",EDGE,"E72.0");var subQ14=sQuery(id+"F12.wireOp",EDGE,"E72.1");var subQ16=sQuery(id+"F12.wireOp",EDGE,"E74.1");var subQ18=sQuery(id+"F12.wireOp",EDGE,"E74.8");Q0=qUnion([makeQuery(id+"F12.imprint","IMPRINT",FACE,{"disambiguationData":[TD([[makeQuery(id+"F12.imprint","IMPRINT",EDGE,{"derivedFrom":subQ7}),1.0]])]}),makeQuery(id+"F12.imprint","IMPRINT",FACE,{"disambiguationData":[TD([[makeQuery(id+"F12.imprint","IMPRINT",EDGE,{"derivedFrom":subQ14}),1.0]])]}),makeQuery(id+"F12.imprint","IMPRINT",FACE,{"disambiguationData":[TD([[makeQuery(id+"F12.imprint","IMPRINT",EDGE,{"derivedFrom":subQ16}),1.0]])]}),makeQuery(id+"F12.imprint","IMPRINT",FACE,{"disambiguationData":[TD([[makeQuery(id+"F12.imprint","IMPRINT",EDGE,{"derivedFrom":subQ18}),-1.0]])]})]);}
            var Q1;
            Q1=makeQuery(id+"F5.boolean.opBoolean","SPLIT",FACE,{"disambiguationData":[TD([makeQuery(id+"F5.opExtrude","SWEPT_FACE",FACE,{"disambiguationData":[OSD([sQuery(id+"F4.wireOp",EDGE,"E41")])]})])],"derivedFrom":makeQuery(id+"F3.boolean.opBoolean","COPY",FACE,{"derivedFrom":makeQuery(id+"F3.opExtrude","CAP_FACE",FACE,{"disambiguationData":[OSD([sQuery(id+"F0.wireOp",EDGE,"E25.0"),sQuery(id+"F0.wireOp",EDGE,"E25.1"),sQuery(id+"F0.wireOp",EDGE,"E25.2"),sQuery(id+"F0.wireOp",EDGE,"E25.3"),sQuery(id+"F0.wireOp",EDGE,"E25.4"),sQuery(id+"F0.wireOp",EDGE,"E25.5"),sQuery(id+"F0.wireOp",EDGE,"E25.6"),sQuery(id+"F0.wireOp",EDGE,"E25.7")])],"isStart":false})})});
            extrude(context, id + "F13", {"entities" : qUnion([Q0]), "operationType" : NewBodyOperationType.REMOVE, "endBound" : BoundingType.UP_TO_SURFACE, "endBoundEntityFace" : qUnion([Q1]), "depth" : 25 * mm});
        }
        {
            var Q0;
            Q0=makeQuery(id+"F3.boolean.opBoolean","COPY",EDGE,{"derivedFrom":makeQuery(id+"F3.opExtrude","CAP_EDGE",EDGE,{"disambiguationData":[OSD([sQuery(id+"F0.wireOp",EDGE,"E25.6")])],"isStart":false})});
            var Q1;
            Q1=makeQuery(id+"F8.boolean.opBoolean","INTERSECT",EDGE,{"derivedFrom":[makeQuery(id+"F5.opExtrude","SWEPT_FACE",FACE,{"disambiguationData":[OSD([sQuery(id+"F4.wireOp",EDGE,"E30")])]}),makeQuery(id+"F8.opExtrude","CAP_FACE",FACE,{"disambiguationData":[OSD([sQuery(id+"F7.wireOp",EDGE,"E67")])],"isStart":false})]});
            var Q2;
            Q2=makeQuery(id+"F8.boolean.opBoolean","INTERSECT",EDGE,{"disambiguationData":[OD(1.0)],"derivedFrom":[makeQuery(id+"F5.opExtrude","SWEPT_FACE",FACE,{"disambiguationData":[OSD([sQuery(id+"F4.wireOp",EDGE,"E30")])]}),makeQuery(id+"F8.opExtrude","SWEPT_FACE",FACE,{"disambiguationData":[OSD([sQuery(id+"F7.wireOp",EDGE,"E67")])]})]});
            var Q3;
            {var subQ0=sQuery(id+"F4.wireOp",EDGE,"E30");Q3=makeQuery(id+"F8.boolean.opBoolean","SPLIT",EDGE,{"disambiguationData":[TD([makeQuery(id+"F5.opExtrude","SWEPT_FACE",FACE,{"disambiguationData":[OSD([sQuery(id+"F4.wireOp",EDGE,"E35.filletArc")])]})])],"derivedFrom":makeQuery(id+"F5.opExtrude","CAP_EDGE",EDGE,{"disambiguationData":[OSD([subQ0])],"isStart":false})});}
            var Q4;
            {var subQ0=sQuery(id+"F0.wireOp",EDGE,"E25.7");var subQ1=sQuery(id+"F0.wireOp",EDGE,"E25.1");var subQ2=sQuery(id+"F0.wireOp",EDGE,"E25.6");var subQ3=sQuery(id+"F0.wireOp",EDGE,"E25.5");var subQ4=sQuery(id+"F0.wireOp",EDGE,"E25.4");var subQ5=sQuery(id+"F0.wireOp",EDGE,"E25.0");var subQ6=sQuery(id+"F0.wireOp",EDGE,"E25.2");var subQ7=sQuery(id+"F0.wireOp",EDGE,"E25.3");Q4=makeQuery(id+"F8.boolean.opBoolean","INTERSECT",EDGE,{"derivedFrom":[makeQuery(id+"F5.boolean.opBoolean","SPLIT",FACE,{"disambiguationData":[TD([makeQuery(id+"F2.opExtrude","SWEPT_FACE",FACE,{"disambiguationData":[OSD([subQ5])]})])],"derivedFrom":makeQuery(id+"F3.boolean.opBoolean","COPY",FACE,{"derivedFrom":makeQuery(id+"F3.opExtrude","CAP_FACE",FACE,{"disambiguationData":[OSD([subQ5,subQ1,subQ6,subQ7,subQ4,subQ3,subQ2,subQ0])],"isStart":false})})}),makeQuery(id+"F8.opExtrude","SWEPT_FACE",FACE,{"disambiguationData":[OSD([sQuery(id+"F7.wireOp",EDGE,"E67")])]})]});}
            var Q5;
            Q5=makeQuery(id+"F8.boolean.opBoolean","INTERSECT",EDGE,{"disambiguationData":[OD(0.0)],"derivedFrom":[makeQuery(id+"F5.opExtrude","SWEPT_FACE",FACE,{"disambiguationData":[OSD([sQuery(id+"F4.wireOp",EDGE,"E30")])]}),makeQuery(id+"F8.opExtrude","SWEPT_FACE",FACE,{"disambiguationData":[OSD([sQuery(id+"F7.wireOp",EDGE,"E67")])]})]});
            fillet(context, id + "F14", {"entities" : qUnion([Q0, Q1, Q2, Q3, Q4, Q5]), "radius" : 3 * mm, "tangentPropagation" : true, "allowEdgeOverflow" : false});
        }
        {
            var Q0;
            Q0=makeQuery(id+"F1.opExtrude","CAP_EDGE",EDGE,{"disambiguationData":[OSD([sQuery(id+"F0.wireOp",EDGE,"E1.bottom")])],"isStart":false});
            fillet(context, id + "F15", {"entities" : qUnion([Q0]), "radius" : 2 * mm, "tangentPropagation" : true, "allowEdgeOverflow" : false});
        }
        {
            var Q0;
            {var subQ0=sQuery(id+"F0.wireOp",EDGE,"E21.filletArc");var subQ1=sQuery(id+"F0.wireOp",EDGE,"E7");var subQ2=sQuery(id+"F0.wireOp",EDGE,"E6");var subQ3=sQuery(id+"F0.wireOp",EDGE,"E5");var subQ4=sQuery(id+"F0.wireOp",EDGE,"E4");var subQ5=sQuery(id+"F0.wireOp",EDGE,"E22.filletArc");var subQ6=sQuery(id+"F0.wireOp",EDGE,"E1.bottom");var subQ7=sQuery(id+"F0.wireOp",EDGE,"E1.right");var subQ8=sQuery(id+"F0.wireOp",EDGE,"E1.top");var subQ9=sQuery(id+"F0.wireOp",EDGE,"E1.left");var subQ10=sQuery(id+"F0.wireOp",EDGE,"E23.filletArc");var subQ11=sQuery(id+"F0.wireOp",EDGE,"E24.filletArc");Q0=makeQuery(id+"F2.boolean.opBoolean","SPLIT",FACE,{"disambiguationData":[TD([makeQuery(id+"F1.opExtrude","SWEPT_FACE",FACE,{"disambiguationData":[OSD([subQ6])]})])],"derivedFrom":makeQuery(id+"F1.opExtrude","CAP_FACE",FACE,{"disambiguationData":[OSD([subQ6,subQ8,subQ9,subQ7,subQ4,subQ3,subQ2,subQ1,subQ0,subQ5,subQ10,subQ11])],"isStart":true})});}
            var sketch = newSketch(context, id + "F16", { "sketchPlane" : qUnion([Q0])});
            skLineSegment(sketch, "E79", {"start": v(0, 74.25) * mm, "end": v(0, 104.25) * mm, "construction": true});
            skArc(sketch, "E80", {"start": v(15, 104.25) * mm, "mid": v(0, 119.25) * mm, "end": v(-15, 104.25) * mm});
            skLineSegment(sketch, "E81", {"start": v(15, 104.25) * mm, "end": v(15, 92.25) * mm});
            skLineSegment(sketch, "E82", {"start": v(-15, 104.25) * mm, "end": v(-15, 92.25) * mm});
            skLineSegment(sketch, "E83", {"start": v(-15, 92.25) * mm, "end": v(-33, 74.25) * mm});
            skLineSegment(sketch, "E84", {"start": v(15, 92.25) * mm, "end": v(33, 74.25) * mm});
            skCircle(sketch, "E85", {"center": v(0, 104.25) * mm, "radius": 6 * mm});
            skLineSegment(sketch, "E86", {"start": v(-74.25, 0) * mm, "end": v(74.25, 0) * mm, "construction": true});
            skLineSegment(sketch, "E87.MirrorCS", {"start": v(15, -104.25) * mm, "end": v(15, -92.25) * mm});
            skLineSegment(sketch, "E88.MirrorCS", {"start": v(-15, -104.25) * mm, "end": v(-15, -92.25) * mm});
            skLineSegment(sketch, "E89.MirrorCS", {"start": v(-15, -92.25) * mm, "end": v(-33, -74.25) * mm});
            skLineSegment(sketch, "E90.MirrorCS", {"start": v(15, -92.25) * mm, "end": v(33, -74.25) * mm});
            skCircle(sketch, "E91.MirrorC", {"center": v(0, -104.25) * mm, "radius": 6 * mm});
            skArc(sketch, "E92.MirrorCS", {"start": v(15, -104.25) * mm, "mid": v(0, -119.25) * mm, "end": v(-15, -104.25) * mm});
            skLineSegment(sketch, "E93.MirrorCS", {"start": v(0, -74.25) * mm, "end": v(0, -104.25) * mm, "construction": true});
            skSolve(sketch);
        }
        {
            var Q0;
            Q0=makeQuery(id+"F16.imprint","IMPRINT",FACE,{"disambiguationData":[TD([[makeQuery(id+"F16.imprint","IMPRINT",EDGE,{"derivedFrom":sQuery(id+"F16.wireOp",EDGE,"E87.MirrorCS")}),1.0]])]});
            var Q1;
            Q1=makeQuery(id+"F16.imprint","IMPRINT",FACE,{"disambiguationData":[TD([[makeQuery(id+"F16.imprint","IMPRINT",EDGE,{"derivedFrom":makeQuery(id+"F1.opExtrude","CAP_EDGE",EDGE,{"disambiguationData":[OSD([sQuery(id+"F0.wireOp",EDGE,"E1.left")])],"isStart":true})}),-1.0]])]});
            var Q2;
            Q2=makeQuery(id+"F16.imprint","IMPRINT",FACE,{"disambiguationData":[TD([[makeQuery(id+"F16.imprint","IMPRINT",EDGE,{"derivedFrom":sQuery(id+"F16.wireOp",EDGE,"E80")}),1.0]])]});
            var Q3;
            Q3=makeQuery(id+"F2.opExtrude","CAP_FACE",FACE,{"disambiguationData":[OSD([sQuery(id+"F0.wireOp",EDGE,"E12"),sQuery(id+"F0.wireOp",EDGE,"E13"),sQuery(id+"F0.wireOp",EDGE,"E14"),sQuery(id+"F0.wireOp",EDGE,"E15"),sQuery(id+"F0.wireOp",EDGE,"E17.filletArc"),sQuery(id+"F0.wireOp",EDGE,"E18.filletArc"),sQuery(id+"F0.wireOp",EDGE,"E19.filletArc"),sQuery(id+"F0.wireOp",EDGE,"E20.filletArc"),sQuery(id+"F0.wireOp",EDGE,"E25.0"),sQuery(id+"F0.wireOp",EDGE,"E25.1"),sQuery(id+"F0.wireOp",EDGE,"E25.2"),sQuery(id+"F0.wireOp",EDGE,"E25.3"),sQuery(id+"F0.wireOp",EDGE,"E25.4"),sQuery(id+"F0.wireOp",EDGE,"E25.5"),sQuery(id+"F0.wireOp",EDGE,"E25.6"),sQuery(id+"F0.wireOp",EDGE,"E25.7")])],"isStart":false});
            extrude(context, id + "F17", {"entities" : qUnion([Q0, Q1, Q2]), "endBound" : BoundingType.UP_TO_SURFACE, "endBoundEntityFace" : qUnion([Q3]), "depth" : 25 * mm});
        }
    });
